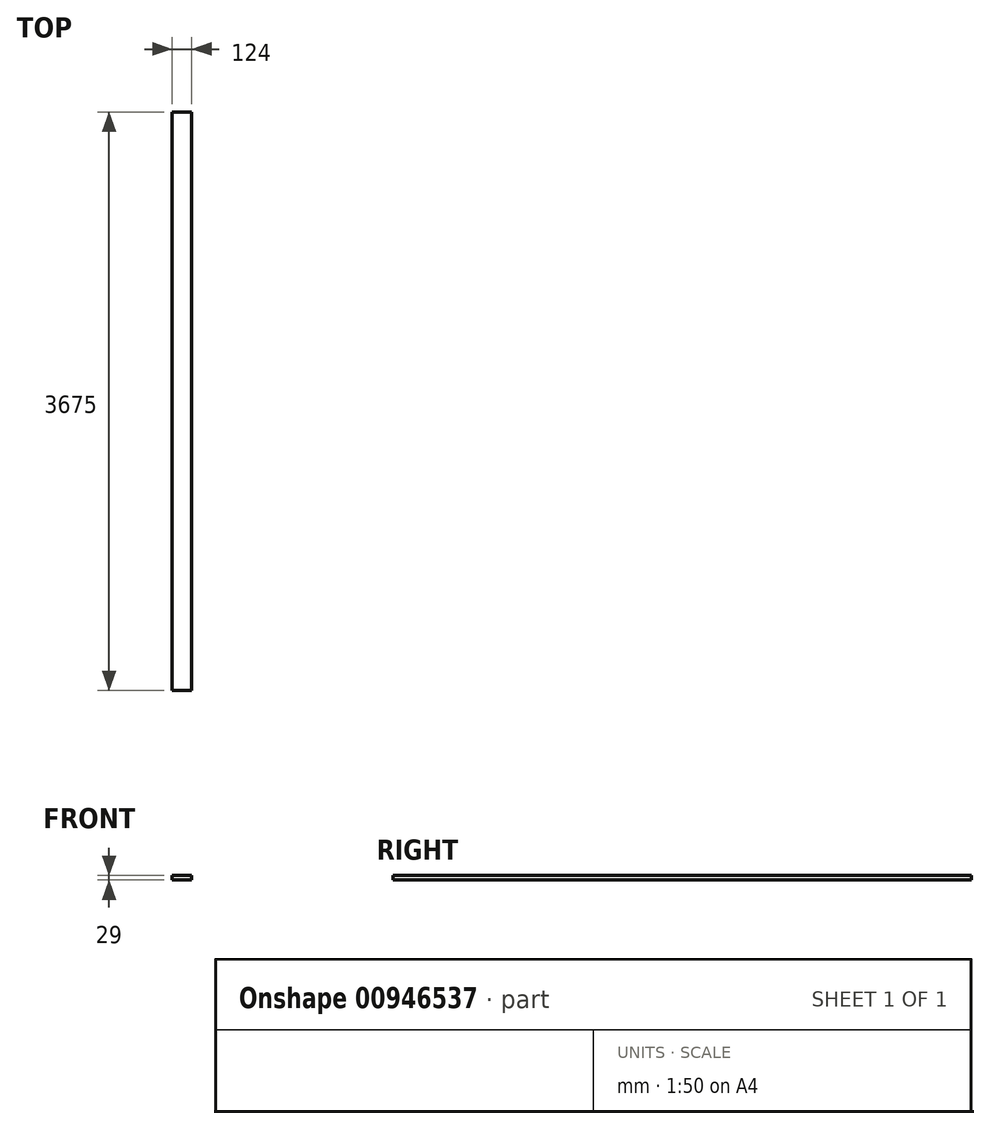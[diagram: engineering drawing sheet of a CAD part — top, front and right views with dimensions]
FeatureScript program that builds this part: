
annotation { "Feature Type Name" : "Feature", "Feature Type Description" : "" }
export const myFeature = defineFeature(function(context is Context, id is Id, definition is map)
    precondition{}
    {
        {
            var Q0;
            Q0=qCreatedBy(makeId("Front.planeOp"),FACE);
            var sketch = newSketch(context, id + "F0", { "sketchPlane" : qUnion([Q0])});
            skLineSegment(sketch, "E0.bottom", {"start": v(0, 0) * mm, "end": v(124, 0) * mm});
            skLineSegment(sketch, "E0.top", {"start": v(0, 29) * mm, "end": v(124, 29) * mm});
            skLineSegment(sketch, "E0.left", {"start": v(0, 0) * mm, "end": v(0, 29) * mm});
            skLineSegment(sketch, "E0.right", {"start": v(124, 0) * mm, "end": v(124, 29) * mm});
            skSolve(sketch);
        }
        {
            var Q0;
            Q0=qSketchRegion(id+"F0",true);
            extrude(context, id + "F1", {"entities" : qUnion([Q0]), "depth" : 3675 * mm, "offsetDistance" : 25 * mm});
        }
    });
